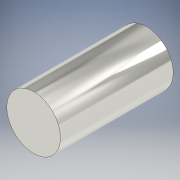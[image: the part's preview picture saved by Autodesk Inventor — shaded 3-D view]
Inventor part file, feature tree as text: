
AUTODESK INVENTOR PART (.ipt)
format: ipt  version: 2021 (Build 250183000, 183)  size: 104,448 bytes
history: native  units: mm
features: extrude x1, sketch x1
ambient origin geometry x8: Origin, YZ Plane, XZ Plane, XY Plane, X Axis, Y Axis, Z Axis, Center Point
bodies: Solid1 (feature_tree)
feature tree (2):
  extrude  "Extrusion1"  Depth=25.4mm TaperAngle=0.0deg
  sketch  "Sketch1"  dims[d0=12.082mm d1=25.4mm d2=0.0mm]
